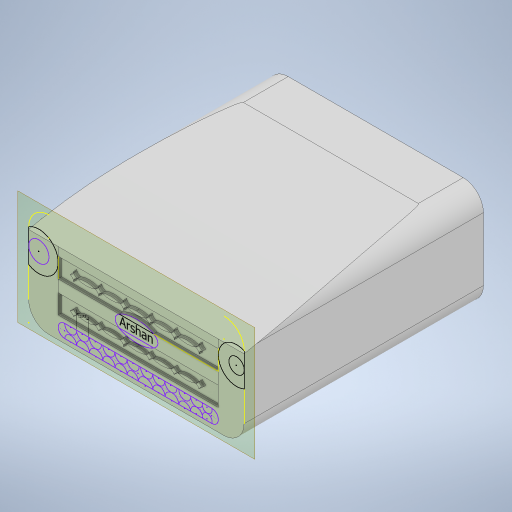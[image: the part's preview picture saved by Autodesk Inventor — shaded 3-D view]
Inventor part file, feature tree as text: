
AUTODESK INVENTOR PART (.ipt)
format: ipt  version: 2024 (Build 280153000, 153)  size: 686,592 bytes
history: native  units: in
note: dims shown in document units (in); Inventor stores cm internally (conversion verified against a paired STEP export)
features: sketch x7, extrude x5, fillet x2, emboss x1, plane x1
ambient origin geometry x8: Origin, YZ Plane, XZ Plane, XY Plane, X Axis, Y Axis, Z Axis, Center Point
bodies: Solid1 (feature_tree)
feature tree (16):
  extrude  "Extrusion1"  Depth=3.194in
  extrude  "Extrusion4"  Depth=2.169in
  fillet  "Fillet3"  Radius=0.504in
  fillet  "Fillet6"  Radius=0.3in
  extrude  "Extrusion5"  Depth=0.103in
  emboss  "Emboss1"
  extrude  "Extrusion11"  Depth=0.101in
  plane  "Work Plane1"
  extrude  "Extrusion12"  Depth=0.0in TaperAngle=0.0deg
  sketch  "Sketch20"  dims[d34=0.05in]
  sketch  "Sketch21"  dims[d38=0.02in d39=0.0in d51=4.0625in d52=0.0in d62=1.5748in d64=1.5748in d66=0.37in d68=0.37in d71=0.05in d72=0.05in d73=0.0in d74=0.0in d75=0.177in d22=0.0in d23=0.0in d25=0.0in d35=0.0in d36=0.0in d37=0.0in d40=0.5in d41=0.0344in d49=0.5in d50=0.0344in d76=0.0344in d77=0.5in d78=0.0344in]
  sketch  "Sketch2"  dims[d0=3.194in d1=3.548in]
  sketch  "Sketch5"  dims[d2=1.536in d3=0.0in d16=2.169in d17=0.792in d18=0.419in d19=0.539in d20=0.504in d21=0.0in d24=0.3in]
  sketch  "Sketch12"  dims[d27=0.2in d28=0.103in]
  sketch  "Sketch16"  dims[d29=0.103in d30=0.101in]
  sketch  "Sketch18"  dims[d31=0.101in d32=0.0in d33=0.0in]
